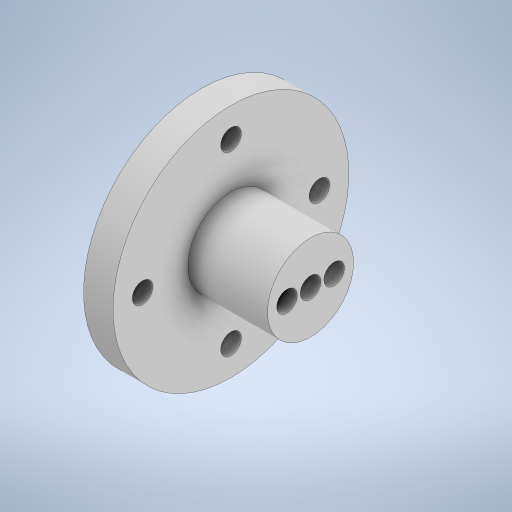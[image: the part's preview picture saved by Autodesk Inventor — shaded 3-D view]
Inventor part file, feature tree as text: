
AUTODESK INVENTOR PART (.ipt)
format: ipt  version: 2023 (Build 270158000, 158)  size: 277,504 bytes
history: native  units: mm
features: extrude x2, sketch x2
ambient origin geometry x8: Origin, YZ Plane, XZ Plane, XY Plane, X Axis, Y Axis, Z Axis, Center Point
bodies: Solid1 (feature_tree)
feature tree (4):
  extrude  "Extrusion1"  Depth=3.5mm
  extrude  "Extrusion5"  Depth=13.5mm
  sketch  "Sketch1"  dims[d0=30.0mm d1=3.5mm]
  sketch  "Sketch5"  dims[d2=40.0mm d4=360.0deg d6=3.5mm d7=40.0mm d8=5.0mm d9=0.0mm d38=8.0mm d39=3.5mm d40=20.0mm d42=360.0deg d44=14.6mm d45=13.5mm d46=0.0mm]
